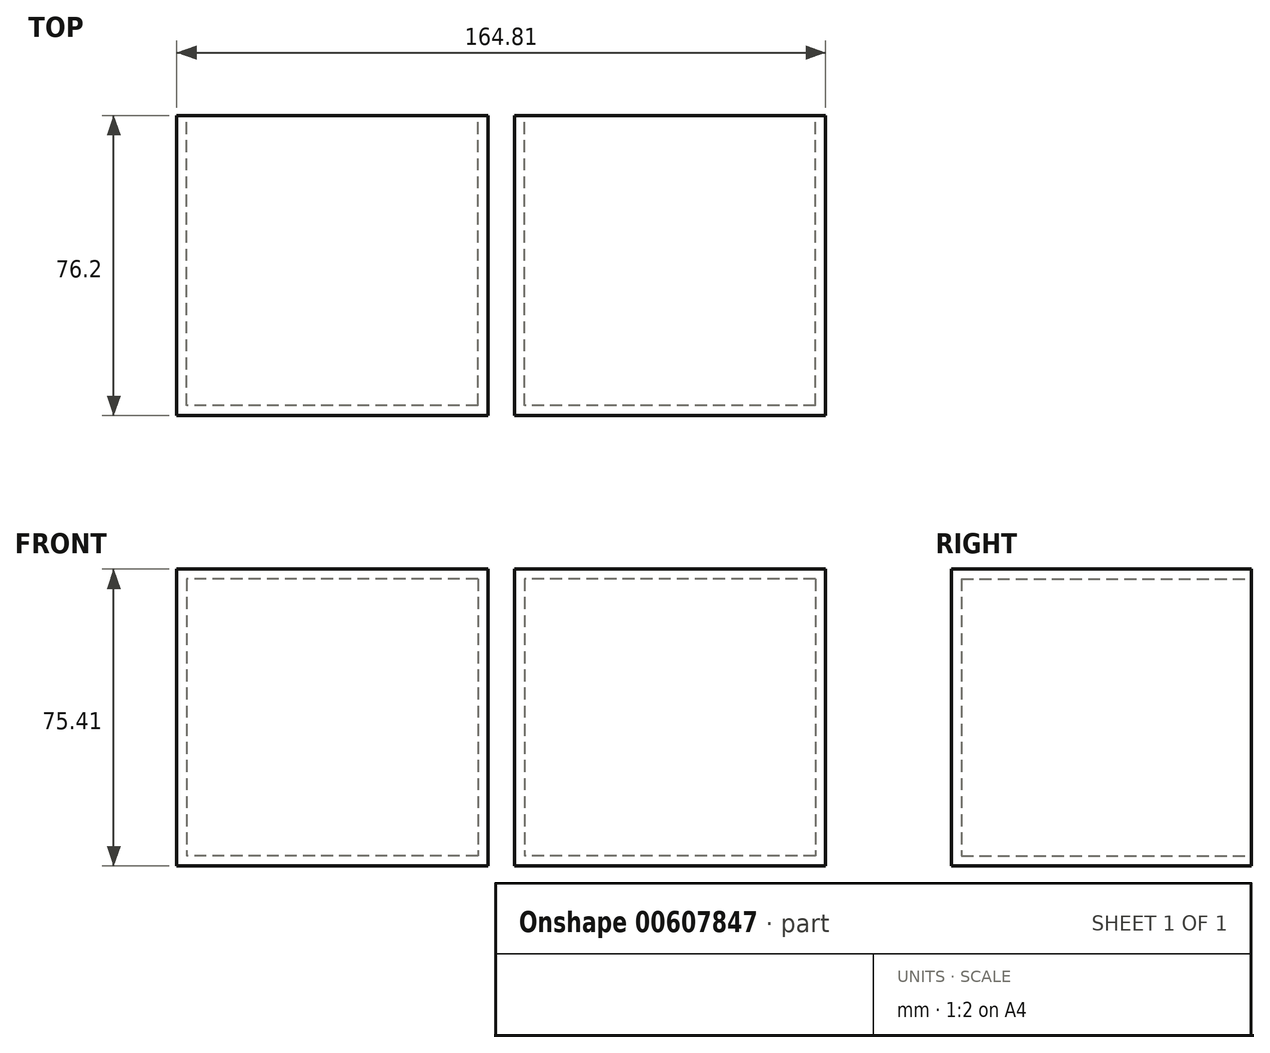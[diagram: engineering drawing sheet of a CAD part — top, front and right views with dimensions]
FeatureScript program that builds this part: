
annotation { "Feature Type Name" : "Feature", "Feature Type Description" : "" }
export const myFeature = defineFeature(function(context is Context, id is Id, definition is map)
    precondition{}
    {
        {
            var Q0;
            Q0=qCreatedBy(makeId("Front.planeOp"),FACE);
            var sketch = newSketch(context, id + "F0", { "sketchPlane" : qUnion([Q0])});
            skLineSegment(sketch, "E0.bottom", {"start": v(85.79, 52.3) * mm, "end": v(6.77, 52.3) * mm});
            skLineSegment(sketch, "E0.top", {"start": v(85.79, -23.1) * mm, "end": v(6.77, -23.1) * mm});
            skLineSegment(sketch, "E0.left", {"start": v(85.79, 52.3) * mm, "end": v(85.79, -23.1) * mm});
            skLineSegment(sketch, "E0.right", {"start": v(6.77, 52.3) * mm, "end": v(6.77, -23.1) * mm});
            skLineSegment(sketch, "E1.bottom", {"start": v(0, 52.3) * mm, "end": v(-79.02, 52.3) * mm});
            skLineSegment(sketch, "E1.top", {"start": v(0, -23.1) * mm, "end": v(-79.02, -23.1) * mm});
            skLineSegment(sketch, "E1.left", {"start": v(0, 52.3) * mm, "end": v(0, -23.1) * mm});
            skLineSegment(sketch, "E1.right", {"start": v(-79.02, 52.3) * mm, "end": v(-79.02, -23.1) * mm});
            skPoint(sketch, "E1.middle", {"position": v(-39.5, 14.6) * mm});
            skSolve(sketch);
        }
        {
            var Q0;
            Q0 = qSketchRegion(id + "F0", true);
            extrude(context, id + "F1", {"entities" : qUnion([Q0]), "depth" : 76.2 * mm, "offsetDistance" : 25.4 * mm});
        }
        {
            var Q0;
            Q0=makeQuery(id+"F1.opExtrude","CAP_FACE",FACE,{"disambiguationData":[OSD([sQuery(id+"F0.wireOp",EDGE,"E0.bottom"),sQuery(id+"F0.wireOp",EDGE,"E0.top"),sQuery(id+"F0.wireOp",EDGE,"E0.left"),sQuery(id+"F0.wireOp",EDGE,"E0.right")])],"isStart":true});
            shell(context, id + "F2", {"entities" : qUnion([Q0]), "thickness" : 2.54 * mm});
        }
        {
            var Q0;
            Q0=makeQuery(id+"F1.opExtrude","CAP_FACE",FACE,{"disambiguationData":[OSD([sQuery(id+"F0.wireOp",EDGE,"E1.bottom"),sQuery(id+"F0.wireOp",EDGE,"E1.top"),sQuery(id+"F0.wireOp",EDGE,"E1.left"),sQuery(id+"F0.wireOp",EDGE,"E1.right")])],"isStart":true});
            shell(context, id + "F3", {"entities" : qUnion([Q0]), "thickness" : 2.54 * mm});
        }
    });
